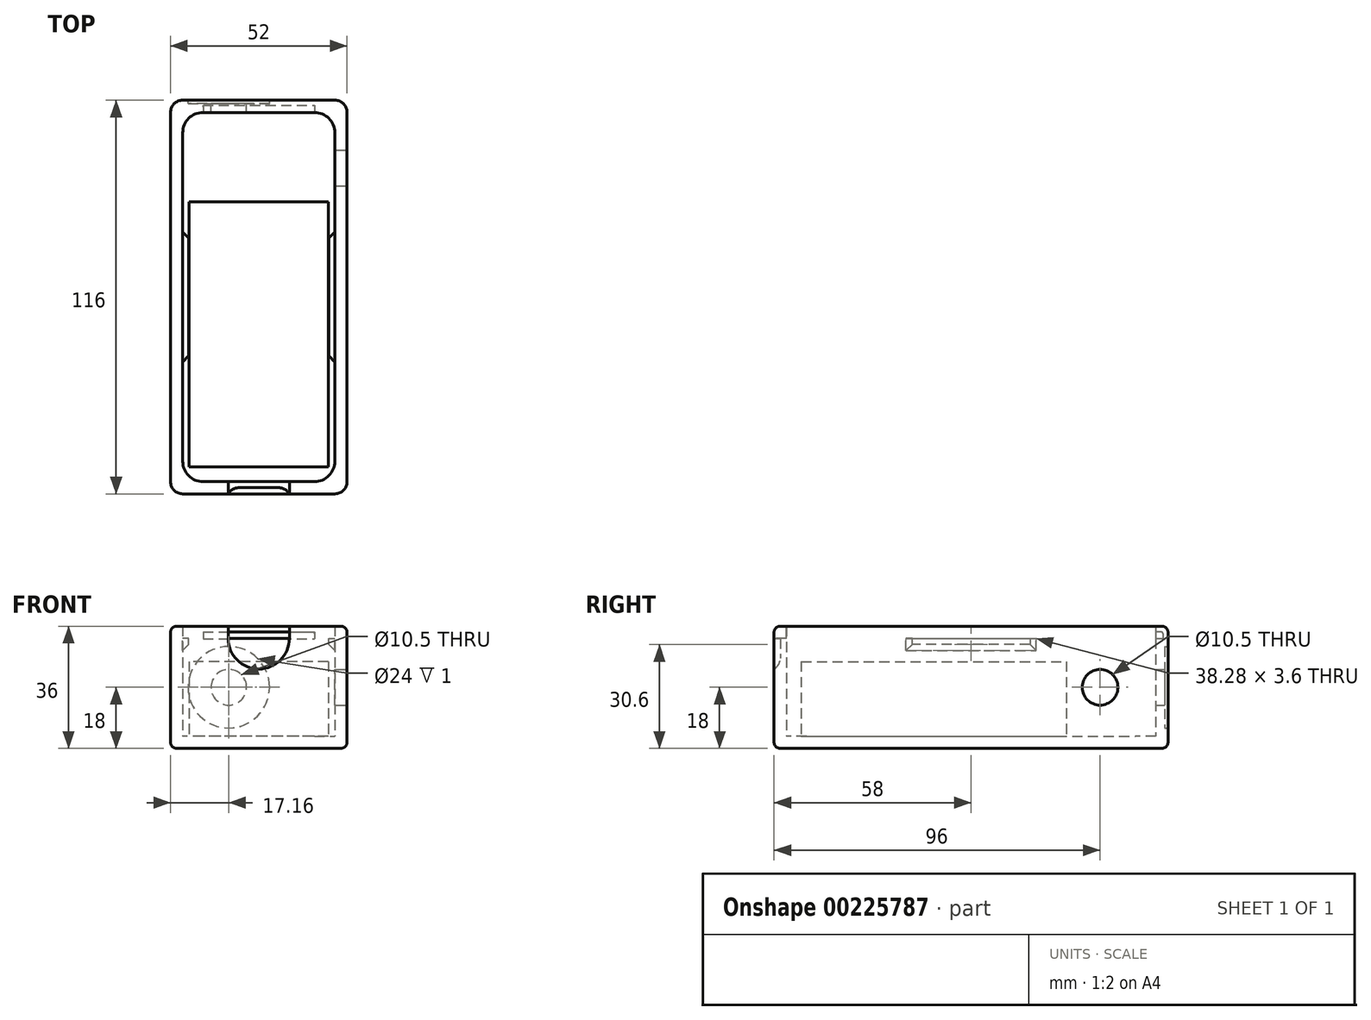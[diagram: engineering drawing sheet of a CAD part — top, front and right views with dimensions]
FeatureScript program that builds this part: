
annotation { "Feature Type Name" : "Feature", "Feature Type Description" : "" }
export const myFeature = defineFeature(function(context is Context, id is Id, definition is map)
    precondition{}
    {
        {
            assignVariable(context, id + "F0", {"name" : "O", "anyValue" : 3.6});
        }
        {
            assignVariable(context, id + "F1", {"name" : "H", "anyValue" : 36});
        }
        {
            var Q0;
            Q0=qCreatedBy(makeId("Top.planeOp"),FACE);
            var sketch = newSketch(context, id + "F2", { "sketchPlane" : qUnion([Q0])});
            skLineSegment(sketch, "E0.bottom", {"start": v(26, -58) * mm, "end": v(-26, -58) * mm});
            skLineSegment(sketch, "E0.top", {"start": v(26, 58) * mm, "end": v(-26, 58) * mm});
            skLineSegment(sketch, "E0.left", {"start": v(26, -58) * mm, "end": v(26, 58) * mm});
            skLineSegment(sketch, "E0.right", {"start": v(-26, -58) * mm, "end": v(-26, 58) * mm});
            skPoint(sketch, "E0.middle", {"position": v(0, 0) * mm});
            skLineSegment(sketch, "E1.0", {"start": v(22.4, 54.4) * mm, "end": v(-22.4, 54.4) * mm});
            skLineSegment(sketch, "E1.1", {"start": v(22.4, -54.4) * mm, "end": v(22.4, 54.4) * mm});
            skLineSegment(sketch, "E1.2", {"start": v(22.4, -54.4) * mm, "end": v(-22.4, -54.4) * mm});
            skLineSegment(sketch, "E1.3", {"start": v(-22.4, -54.4) * mm, "end": v(-22.4, 54.4) * mm});
            skSolve(sketch);
        }
        {
            var Q0;
            Q0=makeQuery(id+"F2.imprint","IMPRINT",FACE,{"disambiguationData":[TD([[makeQuery(id+"F2.imprint","IMPRINT",EDGE,{"derivedFrom":sQuery(id+"F2.wireOp",EDGE,"E0.bottom")}),-1.0]])]});
            extrude(context, id + "F3", {"entities" : qUnion([Q0]), "depth" : (getVariable(context, 'H')) * mm});
        }
        {
            var Q0;
            Q0=makeQuery(id+"F2.imprint","IMPRINT",FACE,{"disambiguationData":[TD([[makeQuery(id+"F2.imprint","IMPRINT",EDGE,{"derivedFrom":sQuery(id+"F2.wireOp",EDGE,"E1.0")}),1.0]])]});
            extrude(context, id + "F4", {"entities" : qUnion([Q0]), "operationType" : NewBodyOperationType.ADD, "depth" : (getVariable(context, 'O')) * mm});
        }
        {
            var Q0;
            Q0=makeQuery(id+"F3.opExtrude","SWEPT_FACE",FACE,{"disambiguationData":[OSD([sQuery(id+"F2.wireOp",EDGE,"E0.left")])]});
            var sketch = newSketch(context, id + "F5", { "sketchPlane" : qUnion([Q0])});
            skCircle(sketch, "E2", {"center": v(38, 18) * mm, "radius": 5.25 * mm});
            skSolve(sketch);
        }
        {
            var Q0;
            Q0=makeQuery(id+"F3.opExtrude","SWEPT_FACE",FACE,{"disambiguationData":[OSD([sQuery(id+"F2.wireOp",EDGE,"E0.top")])]});
            var sketch = newSketch(context, id + "F6", { "sketchPlane" : qUnion([Q0])});
            skCircle(sketch, "E3", {"center": v(8.84, 18) * mm, "radius": 5.25 * mm});
            skCircle(sketch, "E4", {"center": v(8.84, 18) * mm, "radius": 12 * mm});
            skSolve(sketch);
        }
        {
            var Q0;
            Q0=makeQuery(id+"F3.opExtrude","SWEPT_EDGE",EDGE,{"disambiguationData":[OSD([sQuery(id+"F2.wireOp",EDGE,"E0.top"),sQuery(id+"F2.wireOp",EDGE,"E0.left")])]});
            var Q1;
            Q1=makeQuery(id+"F3.opExtrude","SWEPT_EDGE",EDGE,{"disambiguationData":[OSD([sQuery(id+"F2.wireOp",EDGE,"E0.top"),sQuery(id+"F2.wireOp",EDGE,"E0.right")])]});
            var Q2;
            Q2=makeQuery(id+"F3.opExtrude","SWEPT_EDGE",EDGE,{"disambiguationData":[OSD([sQuery(id+"F2.wireOp",EDGE,"E0.bottom"),sQuery(id+"F2.wireOp",EDGE,"E0.right")])]});
            var Q3;
            Q3=makeQuery(id+"F3.opExtrude","SWEPT_EDGE",EDGE,{"disambiguationData":[OSD([sQuery(id+"F2.wireOp",EDGE,"E0.bottom"),sQuery(id+"F2.wireOp",EDGE,"E0.left")])]});
            fillet(context, id + "F7", {"entities" : qUnion([Q0, Q1, Q2, Q3]), "radius" : (getVariable(context, 'O')) * mm, "tangentPropagation" : true, "allowEdgeOverflow" : false});
        }
        {
            var Q0;
            Q0=makeQuery(id+"F3.opExtrude","SWEPT_EDGE",EDGE,{"disambiguationData":[OSD([sQuery(id+"F2.wireOp",EDGE,"E1.2"),sQuery(id+"F2.wireOp",EDGE,"E1.3")])]});
            var Q1;
            Q1=makeQuery(id+"F3.opExtrude","SWEPT_EDGE",EDGE,{"disambiguationData":[OSD([sQuery(id+"F2.wireOp",EDGE,"E1.1"),sQuery(id+"F2.wireOp",EDGE,"E1.2")])]});
            var Q2;
            Q2=makeQuery(id+"F3.opExtrude","SWEPT_EDGE",EDGE,{"disambiguationData":[OSD([sQuery(id+"F2.wireOp",EDGE,"E1.0"),sQuery(id+"F2.wireOp",EDGE,"E1.1")])]});
            var Q3;
            Q3=makeQuery(id+"F3.opExtrude","SWEPT_EDGE",EDGE,{"disambiguationData":[OSD([sQuery(id+"F2.wireOp",EDGE,"E1.0"),sQuery(id+"F2.wireOp",EDGE,"E1.3")])]});
            fillet(context, id + "F8", {"entities" : qUnion([Q0, Q1, Q2, Q3]), "radius" : (getVariable(context, 'O') * 1.67) * mm, "tangentPropagation" : true, "allowEdgeOverflow" : false});
        }
        {
            var Q0;
            Q0=makeQuery(id+"F6.imprint","IMPRINT",FACE,{"disambiguationData":[TD([[makeQuery(id+"F6.imprint","IMPRINT",EDGE,{"derivedFrom":sQuery(id+"F6.wireOp",EDGE,"E3")}),1.0]])]});
            extrude(context, id + "F9", {"entities" : qUnion([Q0]), "operationType" : NewBodyOperationType.REMOVE, "oppositeDirection" : true, "depth" : (getVariable(context, 'O')) * mm});
        }
        {
            var Q0;
            Q0=makeQuery(id+"F5.imprint","IMPRINT",FACE,{"disambiguationData":[TD([[makeQuery(id+"F5.imprint","IMPRINT",EDGE,{"derivedFrom":sQuery(id+"F5.wireOp",EDGE,"E2")}),1.0]])]});
            extrude(context, id + "F10", {"entities" : qUnion([Q0]), "operationType" : NewBodyOperationType.REMOVE, "oppositeDirection" : true, "depth" : (getVariable(context, 'O')) * mm});
        }
        {
            var Q0;
            Q0=makeQuery(id+"F3.opExtrude","SWEPT_FACE",FACE,{"disambiguationData":[OSD([sQuery(id+"F2.wireOp",EDGE,"E0.bottom")])]});
            var sketch = newSketch(context, id + "F11", { "sketchPlane" : qUnion([Q0])});
            skLineSegment(sketch, "E5.bottom", {"start": v(9, 32.4) * mm, "end": v(-9, 32.4) * mm});
            skLineSegment(sketch, "E5.top", {"start": v(9, 36) * mm, "end": v(-9, 36) * mm});
            skLineSegment(sketch, "E5.left", {"start": v(9, 32.4) * mm, "end": v(9, 36) * mm});
            skLineSegment(sketch, "E5.right", {"start": v(-9, 32.4) * mm, "end": v(-9, 36) * mm});
            skPoint(sketch, "E5.middle", {"position": v(0, 34.2) * mm});
            skPoint(sketch, "E5.middle.positionSnap0", {"position": v(0, 0) * mm});
            skPoint(sketch, "E5.centerSnap0", {"position": v(0, 0) * mm});
            skArc(sketch, "E6", {"start": v(-9, 32.4) * mm, "mid": v(0, 23.4) * mm, "end": v(9, 32.4) * mm});
            skSolve(sketch);
        }
        {
            var Q0;
            Q0=makeQuery(id+"F11.imprint","IMPRINT",FACE,{"disambiguationData":[TD([[makeQuery(id+"F11.imprint","IMPRINT",EDGE,{"derivedFrom":sQuery(id+"F11.wireOp",EDGE,"E5.bottom")}),-1.0]])]});
            extrude(context, id + "F12", {"entities" : qUnion([Q0]), "operationType" : NewBodyOperationType.REMOVE, "oppositeDirection" : true, "depth" : (getVariable(context, 'O')) * mm});
        }
        {
            var Q0;
            Q0=makeQuery(id+"F3.opExtrude","SWEPT_FACE",FACE,{"disambiguationData":[OSD([sQuery(id+"F2.wireOp",EDGE,"E1.0")])]});
            var sketch = newSketch(context, id + "F13", { "sketchPlane" : qUnion([Q0])});
            skLineSegment(sketch, "E7.bottom", {"start": v(-16.4, 34.3) * mm, "end": v(16.4, 34.3) * mm});
            skLineSegment(sketch, "E7.top", {"start": v(-16.4, 32.3) * mm, "end": v(16.4, 32.3) * mm});
            skLineSegment(sketch, "E7.left", {"start": v(-16.4, 34.3) * mm, "end": v(-16.4, 32.3) * mm});
            skLineSegment(sketch, "E7.right", {"start": v(16.4, 34.3) * mm, "end": v(16.4, 32.3) * mm});
            skSolve(sketch);
        }
        {
            var Q0;
            Q0=makeQuery(id+"F13.imprint","IMPRINT",FACE,{"disambiguationData":[TD([[makeQuery(id+"F13.imprint","IMPRINT",EDGE,{"derivedFrom":sQuery(id+"F13.wireOp",EDGE,"E7.bottom")}),-1.0]])]});
            extrude(context, id + "F14", {"entities" : qUnion([Q0]), "operationType" : NewBodyOperationType.REMOVE, "oppositeDirection" : true, "depth" : 2.1 * mm});
        }
        {
            var Q0;
            {var subQ0=sQuery(id+"F2.wireOp",EDGE,"E0.bottom");Q0=makeQuery(id+"F12.boolean.opBoolean","SPLIT",EDGE,{"disambiguationData":[TD([makeQuery(id+"F12.opExtrude","SWEPT_FACE",FACE,{"disambiguationData":[OSD([sQuery(id+"F11.wireOp",EDGE,"E5.left")])]})])],"derivedFrom":makeQuery(id+"F3.opExtrude","CAP_EDGE",EDGE,{"disambiguationData":[OSD([subQ0])],"isStart":false})});}
            var Q1;
            {var subQ0=sQuery(id+"F2.wireOp",EDGE,"E0.left");var subQ1=sQuery(id+"F2.wireOp",EDGE,"E0.bottom");Q1=makeQuery(id+"F7.opFillet","BLEND_EDGE",EDGE,{"blendedFrom":[makeQuery(id+"F3.opExtrude","SWEPT_EDGE",EDGE,{"disambiguationData":[OSD([subQ1,subQ0])]}),makeQuery(id+"F3.opExtrude","CAP_FACE",FACE,{"disambiguationData":[OSD([subQ1,sQuery(id+"F2.wireOp",EDGE,"E0.top"),subQ0,sQuery(id+"F2.wireOp",EDGE,"E0.right"),sQuery(id+"F2.wireOp",EDGE,"E1.0"),sQuery(id+"F2.wireOp",EDGE,"E1.1"),sQuery(id+"F2.wireOp",EDGE,"E1.2"),sQuery(id+"F2.wireOp",EDGE,"E1.3")])],"isStart":false})],"blendedInto":[makeQuery(id+"F3.opExtrude","CAP_FACE",FACE,{"disambiguationData":[OSD([subQ1,sQuery(id+"F2.wireOp",EDGE,"E0.top"),subQ0,sQuery(id+"F2.wireOp",EDGE,"E0.right"),sQuery(id+"F2.wireOp",EDGE,"E1.0"),sQuery(id+"F2.wireOp",EDGE,"E1.1"),sQuery(id+"F2.wireOp",EDGE,"E1.2"),sQuery(id+"F2.wireOp",EDGE,"E1.3")])],"isStart":false})]});}
            var Q2;
            Q2=makeQuery(id+"F3.opExtrude","CAP_EDGE",EDGE,{"disambiguationData":[OSD([sQuery(id+"F2.wireOp",EDGE,"E0.left")])],"isStart":false});
            var Q3;
            {var subQ0=sQuery(id+"F2.wireOp",EDGE,"E0.bottom");Q3=makeQuery(id+"F12.boolean.opBoolean","SPLIT",EDGE,{"disambiguationData":[TD([makeQuery(id+"F12.opExtrude","SWEPT_FACE",FACE,{"disambiguationData":[OSD([sQuery(id+"F11.wireOp",EDGE,"E5.right")])]})])],"derivedFrom":makeQuery(id+"F3.opExtrude","CAP_EDGE",EDGE,{"disambiguationData":[OSD([subQ0])],"isStart":false})});}
            var Q4;
            {var subQ0=sQuery(id+"F2.wireOp",EDGE,"E0.right");var subQ1=sQuery(id+"F2.wireOp",EDGE,"E0.bottom");Q4=makeQuery(id+"F7.opFillet","BLEND_EDGE",EDGE,{"blendedFrom":[makeQuery(id+"F3.opExtrude","SWEPT_EDGE",EDGE,{"disambiguationData":[OSD([subQ1,subQ0])]}),makeQuery(id+"F3.opExtrude","CAP_FACE",FACE,{"disambiguationData":[OSD([subQ1,sQuery(id+"F2.wireOp",EDGE,"E0.top"),sQuery(id+"F2.wireOp",EDGE,"E0.left"),subQ0,sQuery(id+"F2.wireOp",EDGE,"E1.0"),sQuery(id+"F2.wireOp",EDGE,"E1.1"),sQuery(id+"F2.wireOp",EDGE,"E1.2"),sQuery(id+"F2.wireOp",EDGE,"E1.3")])],"isStart":false})],"blendedInto":[makeQuery(id+"F3.opExtrude","CAP_FACE",FACE,{"disambiguationData":[OSD([subQ1,sQuery(id+"F2.wireOp",EDGE,"E0.top"),sQuery(id+"F2.wireOp",EDGE,"E0.left"),subQ0,sQuery(id+"F2.wireOp",EDGE,"E1.0"),sQuery(id+"F2.wireOp",EDGE,"E1.1"),sQuery(id+"F2.wireOp",EDGE,"E1.2"),sQuery(id+"F2.wireOp",EDGE,"E1.3")])],"isStart":false})]});}
            var Q5;
            Q5=makeQuery(id+"F3.opExtrude","CAP_EDGE",EDGE,{"disambiguationData":[OSD([sQuery(id+"F2.wireOp",EDGE,"E0.right")])],"isStart":false});
            var Q6;
            {var subQ0=sQuery(id+"F2.wireOp",EDGE,"E0.right");var subQ1=sQuery(id+"F2.wireOp",EDGE,"E0.top");Q6=makeQuery(id+"F7.opFillet","BLEND_EDGE",EDGE,{"blendedFrom":[makeQuery(id+"F3.opExtrude","SWEPT_EDGE",EDGE,{"disambiguationData":[OSD([subQ1,subQ0])]}),makeQuery(id+"F3.opExtrude","CAP_FACE",FACE,{"disambiguationData":[OSD([sQuery(id+"F2.wireOp",EDGE,"E0.bottom"),subQ1,sQuery(id+"F2.wireOp",EDGE,"E0.left"),subQ0,sQuery(id+"F2.wireOp",EDGE,"E1.0"),sQuery(id+"F2.wireOp",EDGE,"E1.1"),sQuery(id+"F2.wireOp",EDGE,"E1.2"),sQuery(id+"F2.wireOp",EDGE,"E1.3")])],"isStart":false})],"blendedInto":[makeQuery(id+"F3.opExtrude","CAP_FACE",FACE,{"disambiguationData":[OSD([sQuery(id+"F2.wireOp",EDGE,"E0.bottom"),subQ1,sQuery(id+"F2.wireOp",EDGE,"E0.left"),subQ0,sQuery(id+"F2.wireOp",EDGE,"E1.0"),sQuery(id+"F2.wireOp",EDGE,"E1.1"),sQuery(id+"F2.wireOp",EDGE,"E1.2"),sQuery(id+"F2.wireOp",EDGE,"E1.3")])],"isStart":false})]});}
            var Q7;
            Q7=makeQuery(id+"F3.opExtrude","CAP_EDGE",EDGE,{"disambiguationData":[OSD([sQuery(id+"F2.wireOp",EDGE,"E0.top")])],"isStart":false});
            var Q8;
            {var subQ0=sQuery(id+"F2.wireOp",EDGE,"E0.left");var subQ1=sQuery(id+"F2.wireOp",EDGE,"E0.top");Q8=makeQuery(id+"F7.opFillet","BLEND_EDGE",EDGE,{"blendedFrom":[makeQuery(id+"F3.opExtrude","SWEPT_EDGE",EDGE,{"disambiguationData":[OSD([subQ1,subQ0])]}),makeQuery(id+"F3.opExtrude","CAP_FACE",FACE,{"disambiguationData":[OSD([sQuery(id+"F2.wireOp",EDGE,"E0.bottom"),subQ1,subQ0,sQuery(id+"F2.wireOp",EDGE,"E0.right"),sQuery(id+"F2.wireOp",EDGE,"E1.0"),sQuery(id+"F2.wireOp",EDGE,"E1.1"),sQuery(id+"F2.wireOp",EDGE,"E1.2"),sQuery(id+"F2.wireOp",EDGE,"E1.3")])],"isStart":false})],"blendedInto":[makeQuery(id+"F3.opExtrude","CAP_FACE",FACE,{"disambiguationData":[OSD([sQuery(id+"F2.wireOp",EDGE,"E0.bottom"),subQ1,subQ0,sQuery(id+"F2.wireOp",EDGE,"E0.right"),sQuery(id+"F2.wireOp",EDGE,"E1.0"),sQuery(id+"F2.wireOp",EDGE,"E1.1"),sQuery(id+"F2.wireOp",EDGE,"E1.2"),sQuery(id+"F2.wireOp",EDGE,"E1.3")])],"isStart":false})]});}
            fillet(context, id + "F15", {"entities" : qUnion([Q0, Q1, Q2, Q3, Q4, Q5, Q6, Q7, Q8]), "radius" : (getVariable(context, 'O') / 2) * mm, "tangentPropagation" : true, "allowEdgeOverflow" : false});
        }
        {
            var Q0;
            {var subQ0=sQuery(id+"F2.wireOp",EDGE,"E1.3");var subQ1=sQuery(id+"F2.wireOp",EDGE,"E1.2");var subQ2=sQuery(id+"F2.wireOp",EDGE,"E1.1");var subQ3=sQuery(id+"F2.wireOp",EDGE,"E1.0");Q0=makeQuery(id+"F4.boolean.opBoolean","MERGE",FACE,{"derivedFrom":[makeQuery(id+"F3.opExtrude","CAP_FACE",FACE,{"disambiguationData":[OSD([sQuery(id+"F2.wireOp",EDGE,"E0.bottom"),sQuery(id+"F2.wireOp",EDGE,"E0.top"),sQuery(id+"F2.wireOp",EDGE,"E0.left"),sQuery(id+"F2.wireOp",EDGE,"E0.right"),subQ3,subQ2,subQ1,subQ0])],"isStart":true}),makeQuery(id+"F4.opExtrude","CAP_FACE",FACE,{"disambiguationData":[OSD([subQ3,subQ2,subQ1,subQ0])],"isStart":true})]});}
            fillet(context, id + "F16", {"entities" : qUnion([Q0]), "radius" : (getVariable(context, 'O') / 2) * mm, "tangentPropagation" : true, "allowEdgeOverflow" : false});
        }
        {
            var Q0;
            Q0=makeQuery(id+"F6.imprint","IMPRINT",FACE,{"disambiguationData":[TD([[makeQuery(id+"F6.imprint","IMPRINT",EDGE,{"derivedFrom":sQuery(id+"F6.wireOp",EDGE,"E3")}),-1.0]])]});
            extrude(context, id + "F17", {"entities" : qUnion([Q0]), "operationType" : NewBodyOperationType.REMOVE, "oppositeDirection" : true, "depth" : 1 * mm});
        }
        {
            var Q0;
            Q0=makeQuery(id+"F14.boolean.opBoolean","COPY",EDGE,{"derivedFrom":makeQuery(id+"F14.opExtrude","CAP_EDGE",EDGE,{"disambiguationData":[OSD([sQuery(id+"F13.wireOp",EDGE,"E7.bottom")])],"isStart":false})});
            fillet(context, id + "F18", {"entities" : qUnion([Q0]), "radius" : 0.5 * mm, "tangentPropagation" : true, "allowEdgeOverflow" : false});
        }
        {
            var Q0;
            Q0=makeQuery(id+"F3.opExtrude","SWEPT_FACE",FACE,{"disambiguationData":[OSD([sQuery(id+"F2.wireOp",EDGE,"E1.1")])]});
            var sketch = newSketch(context, id + "F19", { "sketchPlane" : qUnion([Q0])});
            skLineSegment(sketch, "E8.bottom", {"start": v(19.14, 28.8) * mm, "end": v(-19.14, 28.8) * mm});
            skLineSegment(sketch, "E8.top", {"start": v(19.14, 32.4) * mm, "end": v(-19.14, 32.4) * mm});
            skLineSegment(sketch, "E8.left", {"start": v(19.14, 28.8) * mm, "end": v(19.14, 32.4) * mm});
            skLineSegment(sketch, "E8.right", {"start": v(-19.14, 28.8) * mm, "end": v(-19.14, 32.4) * mm});
            skPoint(sketch, "E8.middle", {"position": v(0, 30.6) * mm});
            skSolve(sketch);
        }
        {
            var Q0;
            Q0=makeQuery(id+"F3.opExtrude","SWEPT_FACE",FACE,{"disambiguationData":[OSD([sQuery(id+"F2.wireOp",EDGE,"E1.3")])]});
            var sketch = newSketch(context, id + "F20", { "sketchPlane" : qUnion([Q0])});
            skLineSegment(sketch, "E9.bottom", {"start": v(19.14, 28.8) * mm, "end": v(-19.14, 28.8) * mm});
            skLineSegment(sketch, "E9.top", {"start": v(19.14, 32.4) * mm, "end": v(-19.14, 32.4) * mm});
            skLineSegment(sketch, "E9.left", {"start": v(19.14, 28.8) * mm, "end": v(19.14, 32.4) * mm});
            skLineSegment(sketch, "E9.right", {"start": v(-19.14, 28.8) * mm, "end": v(-19.14, 32.4) * mm});
            skPoint(sketch, "E9.middle", {"position": v(0, 30.6) * mm});
            skSolve(sketch);
        }
        {
            var Q0;
            Q0=makeQuery(id+"F19.imprint","IMPRINT",FACE,{"disambiguationData":[TD([[makeQuery(id+"F19.imprint","IMPRINT",EDGE,{"derivedFrom":sQuery(id+"F19.wireOp",EDGE,"E8.bottom")}),-1.0]])]});
            extrude(context, id + "F21", {"entities" : qUnion([Q0]), "operationType" : NewBodyOperationType.ADD, "depth" : (getVariable(context, 'O') * .5) * mm});
        }
        {
            var Q0;
            Q0=makeQuery(id+"F20.imprint","IMPRINT",FACE,{"disambiguationData":[TD([[makeQuery(id+"F20.imprint","IMPRINT",EDGE,{"derivedFrom":sQuery(id+"F20.wireOp",EDGE,"E9.bottom")}),-1.0]])]});
            extrude(context, id + "F22", {"entities" : qUnion([Q0]), "operationType" : NewBodyOperationType.ADD, "depth" : (getVariable(context, 'O') * .5) * mm});
        }
        {
            var Q0;
            Q0=makeQuery(id+"F22.opExtrude","CAP_EDGE",EDGE,{"disambiguationData":[OSD([sQuery(id+"F20.wireOp",EDGE,"E9.right")])],"isStart":false});
            var Q1;
            Q1=makeQuery(id+"F22.opExtrude","CAP_EDGE",EDGE,{"disambiguationData":[OSD([sQuery(id+"F20.wireOp",EDGE,"E9.bottom")])],"isStart":false});
            var Q2;
            Q2=makeQuery(id+"F22.opExtrude","CAP_EDGE",EDGE,{"disambiguationData":[OSD([sQuery(id+"F20.wireOp",EDGE,"E9.left")])],"isStart":false});
            var Q3;
            Q3=makeQuery(id+"FUkj4zLFzn2cjNl_1.opExtrude","CAP_EDGE",EDGE,{"disambiguationData":[OSD([sQuery(id+"FduqIQM7QhTX7Re_1.wireOp",EDGE,"Uwhg5jXr-3Yt5-poT9-xr3U-90L54EeIlBer.right")])],"isStart":false});
            var Q4;
            Q4=makeQuery(id+"FUkj4zLFzn2cjNl_1.opExtrude","CAP_EDGE",EDGE,{"disambiguationData":[OSD([sQuery(id+"FduqIQM7QhTX7Re_1.wireOp",EDGE,"Uwhg5jXr-3Yt5-poT9-xr3U-90L54EeIlBer.left")])],"isStart":false});
            var Q5;
            Q5=makeQuery(id+"FUkj4zLFzn2cjNl_1.opExtrude","CAP_EDGE",EDGE,{"disambiguationData":[OSD([sQuery(id+"FduqIQM7QhTX7Re_1.wireOp",EDGE,"Uwhg5jXr-3Yt5-poT9-xr3U-90L54EeIlBer.bottom")])],"isStart":false});
            var Q6;
            Q6=makeQuery(id+"F21.opExtrude","CAP_EDGE",EDGE,{"disambiguationData":[OSD([sQuery(id+"F19.wireOp",EDGE,"E8.right")])],"isStart":false});
            var Q7;
            Q7=makeQuery(id+"F21.opExtrude","CAP_EDGE",EDGE,{"disambiguationData":[OSD([sQuery(id+"F19.wireOp",EDGE,"E8.bottom")])],"isStart":false});
            var Q8;
            Q8=makeQuery(id+"F21.opExtrude","CAP_EDGE",EDGE,{"disambiguationData":[OSD([sQuery(id+"F19.wireOp",EDGE,"E8.left")])],"isStart":false});
            chamfer(context, id + "F23", {"entities" : qUnion([Q0, Q1, Q2, Q3, Q4, Q5, Q6, Q7, Q8]), "width" : (getVariable(context, 'O') * 0.5) * mm, "tangentPropagation" : true});
        }
        {
            var Q0;
            Q0=makeQuery(id+"F3.opExtrude","SWEPT_FACE",FACE,{"disambiguationData":[OSD([sQuery(id+"F2.wireOp",EDGE,"E1.2")])]});
            var sketch = newSketch(context, id + "F24", { "sketchPlane" : qUnion([Q0])});
            skLineSegment(sketch, "E10", {"start": v(-9, 34.4) * mm, "end": v(-20.4, 34.4) * mm});
            skLineSegment(sketch, "E11", {"start": v(9, 34.4) * mm, "end": v(20.4, 34.4) * mm});
            skLineSegment(sketch, "E12", {"start": v(9, 32.4) * mm, "end": v(16.4, 32.4) * mm});
            skLineSegment(sketch, "E13", {"start": v(-9, 32.4) * mm, "end": v(-16.4, 32.4) * mm});
            skSolve(sketch);
        }
        {
            var Q0;
            Q0=makeQuery(id+"F11.imprint","IMPRINT",FACE,{"disambiguationData":[TD([[makeQuery(id+"F11.imprint","IMPRINT",EDGE,{"derivedFrom":sQuery(id+"F11.wireOp",EDGE,"E5.bottom")}),1.0]])]});
            extrude(context, id + "F25", {"entities" : qUnion([Q0]), "operationType" : NewBodyOperationType.REMOVE, "oppositeDirection" : true, "depth" : (getVariable(context, 'O') / 2) * mm});
        }
        {
            var Q0;
            Q0=makeQuery(id+"F25.boolean.opBoolean","COPY",EDGE,{"derivedFrom":makeQuery(id+"F25.opExtrude","CAP_EDGE",EDGE,{"disambiguationData":[OSD([sQuery(id+"F11.wireOp",EDGE,"E6")])],"isStart":false})});
            fillet(context, id + "F26", {"entities" : qUnion([Q0]), "radius" : (getVariable(context, 'O')) * mm, "tangentPropagation" : true, "allowEdgeOverflow" : false});
        }
        {
            var Q0;
            Q0=makeQuery(id+"F4.opExtrude","CAP_FACE",FACE,{"disambiguationData":[OSD([sQuery(id+"F2.wireOp",EDGE,"E1.0"),sQuery(id+"F2.wireOp",EDGE,"E1.1"),sQuery(id+"F2.wireOp",EDGE,"E1.2"),sQuery(id+"F2.wireOp",EDGE,"E1.3")])],"isStart":false});
            var sketch = newSketch(context, id + "F27", { "sketchPlane" : qUnion([Q0])});
            skLineSegment(sketch, "E14.bottom", {"start": v(20.5, -50) * mm, "end": v(-20.5, -50) * mm});
            skLineSegment(sketch, "E14.top", {"start": v(20.5, 28) * mm, "end": v(-20.5, 28) * mm});
            skLineSegment(sketch, "E14.left", {"start": v(20.5, -50) * mm, "end": v(20.5, 28) * mm});
            skLineSegment(sketch, "E14.right", {"start": v(-20.5, -50) * mm, "end": v(-20.5, 28) * mm});
            skPoint(sketch, "E14.middle", {"position": v(0, -11) * mm});
            skSolve(sketch);
        }
        {
            var Q0;
            Q0=makeQuery(id+"F27.imprint","IMPRINT",FACE,{"disambiguationData":[TD([[makeQuery(id+"F27.imprint","IMPRINT",EDGE,{"derivedFrom":sQuery(id+"F27.wireOp",EDGE,"E14.bottom")}),-1.0]])]});
            extrude(context, id + "F28", {"entities" : qUnion([Q0]), "depth" : 22 * mm});
        }
    });
